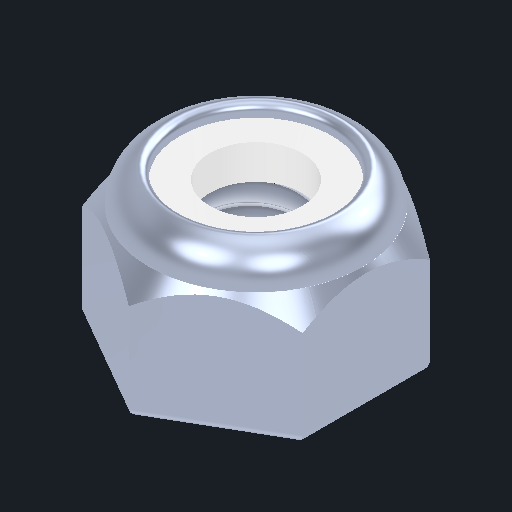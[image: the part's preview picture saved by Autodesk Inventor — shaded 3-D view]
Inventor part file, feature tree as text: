
AUTODESK INVENTOR PART (.ipt)
format: ipt  version: 2024 (Build 280153000, 153)  size: 247,296 bytes
history: native  units: in
note: dims shown in document units (in); Inventor stores cm internally (conversion verified against a paired STEP export)
features: plane x2, other x1, imported_body x1, split x1, thread x1, extrude x1, fillet x1
ambient origin geometry x8: Origin, YZ Plane, XZ Plane, XY Plane, X Axis, Y Axis, Z Axis, Center Point
bodies: Body1 (feature_tree)
feature tree (8):
  parser-record x1  (decoder bookkeeping rows leaked as tree rows — omitted from the tree; the rows remain in map.json)
  imported_body  "Base1"
  plane  "Work Plane1"
  split  "Split1"
  thread  "Thread1"  [1 undecoded]
  plane  "Work Plane2"
  extrude  "Extrusion1"  [1 undecoded]
  fillet  "Fillet1"  Radius=0.053in
note: 2 required parameter values undecoded (feature->parameter linkage not recoverable at this tier; creation-order binding heuristic only, values carry confidence <= 0.55)
